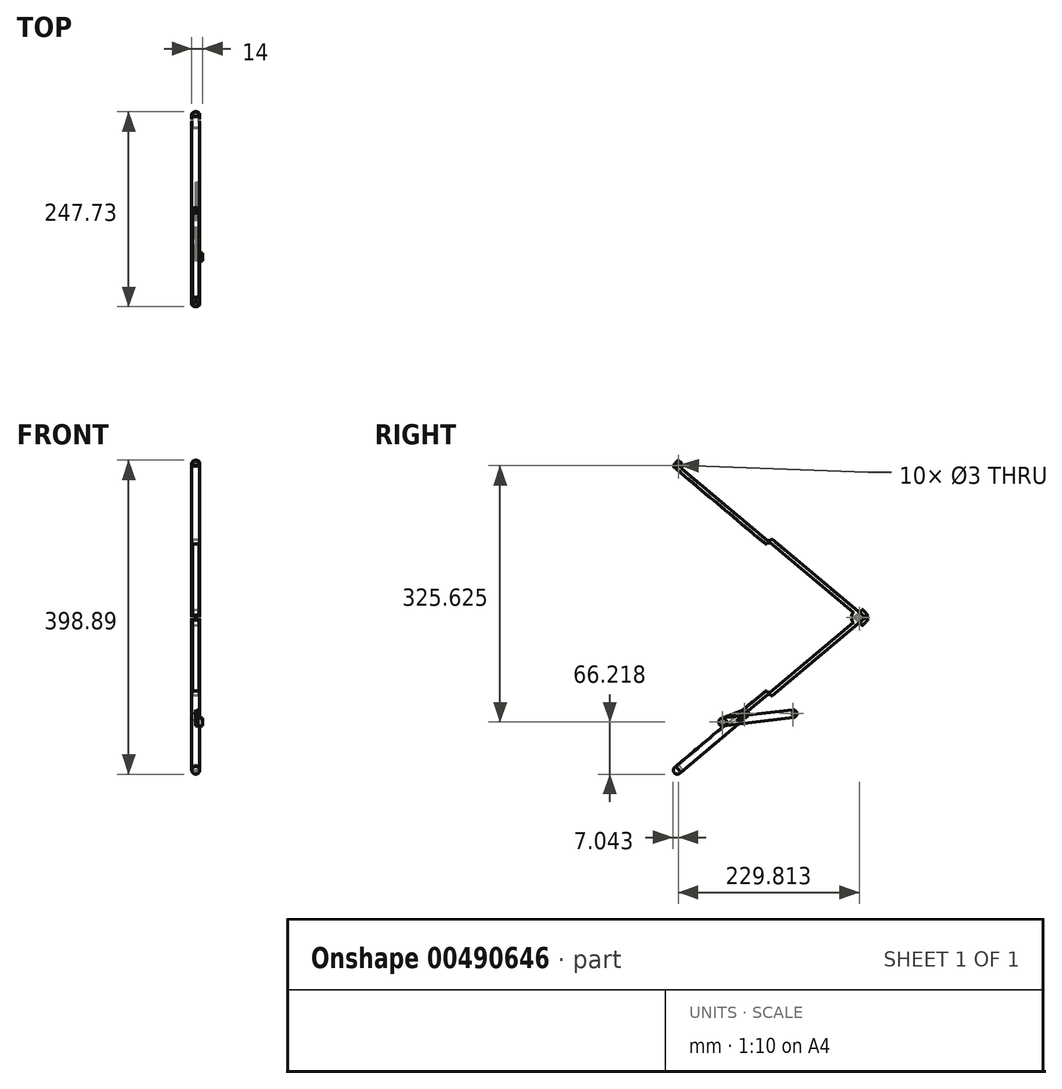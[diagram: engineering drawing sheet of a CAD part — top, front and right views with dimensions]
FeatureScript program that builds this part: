
annotation { "Feature Type Name" : "Feature", "Feature Type Description" : "" }
export const myFeature = defineFeature(function(context is Context, id is Id, definition is map)
    precondition{}
    {
        {
            assignVariable(context, id + "F0", {"name" : "tube_od", "anyValue" : 10});
        }
        {
            var Q0;
            Q0=qCreatedBy(makeId("Right.planeOp"),FACE);
            var sketch = newSketch(context, id + "F1", { "sketchPlane" : qUnion([Q0])});
            skLineSegment(sketch, "E0", {"start": v(114.9, 0) * mm, "end": v(114.9, 664.57) * mm, "construction": true});
            skLineSegment(sketch, "E1", {"start": v(-114.9, 0) * mm, "end": v(-114.9, 664.3) * mm, "construction": true});
            skLineSegment(sketch, "E2", {"start": v(114.9, 5) * mm, "end": v(-114.9, 197.84) * mm});
            skLineSegment(sketch, "E3", {"start": v(-114.9, 197.84) * mm, "end": v(114.9, 390.67) * mm});
            skLineSegment(sketch, "E4", {"start": v(-114.9, 5) * mm, "end": v(114.9, 5) * mm, "construction": true});
            skLineSegment(sketch, "E5", {"start": v(-114.9, 5) * mm, "end": v(114.9, 197.84) * mm});
            skLineSegment(sketch, "E6", {"start": v(114.9, 197.84) * mm, "end": v(-114.9, 390.67) * mm});
            skPoint(sketch, "E7", {"position": v(0, 5) * mm});
            skCircle(sketch, "E8", {"center": v(114.9, 5) * mm, "radius": 5 * mm});
            skLineSegment(sketch, "E9", {"start": v(114.9, 390.67) * mm, "end": v(-114.9, 583.5) * mm});
            skLineSegment(sketch, "E10", {"start": v(-114.9, 390.67) * mm, "end": v(114.9, 583.5) * mm});
            skLineSegment(sketch, "E11", {"start": v(-30.64, 75.7) * mm, "end": v(30.64, 75.7) * mm, "construction": true});
            skLineSegment(sketch, "E12", {"start": v(-30.64, 75.7) * mm, "end": v(-58.68, 65.05) * mm});
            skLineSegment(sketch, "E13", {"start": v(-58.68, 65.05) * mm, "end": v(30.64, 75.7) * mm});
            skPoint(sketch, "E14", {"position": v(0, 101.42) * mm});
            skCircle(sketch, "E15", {"center": v(-30.64, 75.7) * mm, "radius": 30 * mm, "construction": true});
            skPoint(sketch, "E16", {"position": v(-53.62, 56.42) * mm});
            skCircle(sketch, "E17", {"center": v(-53.62, 56.42) * mm, "radius": 5 * mm});
            skCircle(sketch, "E18", {"center": v(-58.68, 65.05) * mm, "radius": 5 * mm});
            skCircle(sketch, "E19", {"center": v(114.9, 197.84) * mm, "radius": 10 * mm});
            skLineSegment(sketch, "E20", {"start": v(114.9, 197.84) * mm, "end": v(122.57, 204.26) * mm});
            skLineSegment(sketch, "E21", {"start": v(114.9, 197.84) * mm, "end": v(122.57, 191.4) * mm});
            skCircle(sketch, "E22", {"center": v(-114.9, 390.67) * mm, "radius": 5 * mm});
            skLineSegment(sketch, "E23", {"start": v(-114.9, 390.67) * mm, "end": v(-118.74, 393.89) * mm});
            skLineSegment(sketch, "E24", {"start": v(-114.9, 5) * mm, "end": v(-111.7, 1.17) * mm});
            skLineSegment(sketch, "E25", {"start": v(-111.7, 1.17) * mm, "end": v(-113.09, 0) * mm});
            skLineSegment(sketch, "E26", {"start": v(-112.34, 1.94) * mm, "end": v(-109.27, 4.5) * mm});
            skLineSegment(sketch, "E27", {"start": v(-109.27, 4.5) * mm, "end": v(-111.84, 7.57) * mm});
            skArc(sketch, "E28", {"start": v(-113.09, 0) * mm, "mid": v(-116.74, -1.15) * mm, "end": v(-120.13, 0.62) * mm});
            skLineSegment(sketch, "E29", {"start": v(-120.13, 0.62) * mm, "end": v(-114.9, 5) * mm});
            skCircle(sketch, "E30", {"center": v(114.9, 197.84) * mm, "radius": 1.5 * mm});
            skCircle(sketch, "E31", {"center": v(0, 101.42) * mm, "radius": 1.5 * mm});
            skCircle(sketch, "E32", {"center": v(0, 294.25) * mm, "radius": 1.5 * mm});
            skCircle(sketch, "E33", {"center": v(-114.9, 390.67) * mm, "radius": 1.5 * mm});
            skSolve(sketch);
        }
        {
            var Q0;
            Q0=sQuery(id+"F1.wireOp",VERTEX,"E5.start");
            var Q1;
            Q1=sQuery(id+"F1.wireOp",EDGE,"E5");
            cPlane(context, id + "F2", {"entities" : qUnion([Q0, Q1]), "cplaneType" : CPlaneType.LINE_POINT, "offset" : 25 * mm, "width" : 150 * mm, "height" : 150 * mm});
        }
        {
            var Q0;
            Q0=qCreatedBy(id+"F2.planeOp",FACE);
            var sketch = newSketch(context, id + "F3", { "sketchPlane" : qUnion([Q0])});
            skPoint(sketch, "E34.0", {"position": v(0, 77.7) * mm});
            skCircle(sketch, "E35", {"center": v(0, 77.7) * mm, "radius": 5 * mm});
            skCircle(sketch, "E36", {"center": v(0, 77.7) * mm, "radius": 4 * mm});
            skSolve(sketch);
        }
        {
            var Q0;
            Q0=makeQuery(id+"F3.imprint","IMPRINT",FACE,{"disambiguationData":[TD([[makeQuery(id+"F3.imprint","IMPRINT",EDGE,{"derivedFrom":sQuery(id+"F3.wireOp",EDGE,"E35")}),1.0]])]});
            var Q1;
            Q1=sQuery(id+"F1.wireOp",EDGE,"E5");
            var Q2;
            Q2=sQuery(id+"F1.wireOp",EDGE,"E20");
            sweep(context, id + "F4", {"profiles" : qUnion([Q0]), "path" : qUnion([Q1, Q2])});
        }
        {
            var Q0;
            Q0=sQuery(id+"F1.wireOp",VERTEX,"E21.end");
            var Q1;
            Q1=sQuery(id+"F1.wireOp",EDGE,"E6");
            cPlane(context, id + "F5", {"entities" : qUnion([Q0, Q1]), "cplaneType" : CPlaneType.LINE_POINT, "offset" : 25 * mm, "width" : 150 * mm, "height" : 150 * mm});
        }
        {
            var Q0;
            Q0=qCreatedBy(id+"F5.planeOp",FACE);
            var sketch = newSketch(context, id + "F6", { "sketchPlane" : qUnion([Q0])});
            skPoint(sketch, "E37.0", {"position": v(0, 225.41) * mm});
            skCircle(sketch, "E38", {"center": v(0, 225.41) * mm, "radius": 5 * mm});
            skCircle(sketch, "E39", {"center": v(0, 225.41) * mm, "radius": 4 * mm});
            skSolve(sketch);
        }
        {
            var Q0;
            Q0=makeQuery(id+"F6.imprint","IMPRINT",FACE,{"disambiguationData":[TD([[makeQuery(id+"F6.imprint","IMPRINT",EDGE,{"derivedFrom":sQuery(id+"F6.wireOp",EDGE,"E38")}),1.0]])]});
            var Q1;
            Q1=sQuery(id+"F1.wireOp",EDGE,"E21");
            var Q2;
            Q2=sQuery(id+"F1.wireOp",EDGE,"E6");
            var Q3;
            Q3=sQuery(id+"F1.wireOp",EDGE,"E23");
            sweep(context, id + "F7", {"profiles" : qUnion([Q0]), "path" : qUnion([Q1, Q2, Q3])});
        }
        {
            var Q0;
            {var subQ0=sQuery(id+"F1.wireOp",EDGE,"E25");Q0=makeQuery(id+"F1.imprint","IMPRINT",FACE,{"disambiguationData":[TD([[makeQuery(id+"F1.imprint","IMPRINT",EDGE,{"derivedFrom":subQ0}),-1.0]])]});}
            var Q1;
            {var subQ4=sQuery(id+"F1.wireOp",EDGE,"E26");Q1=makeQuery(id+"F1.imprint","IMPRINT",FACE,{"disambiguationData":[TD([[makeQuery(id+"F1.imprint","IMPRINT",EDGE,{"derivedFrom":subQ4}),1.0]])]});}
            var Q2;
            Q2=sQuery(id+"F1.wireOp",EDGE,"E5");
            revolve(context, id + "F8", {"entities" : qUnion([Q0, Q1]), "axis" : qUnion([Q2]), "revolveType" : RevolveType.FULL});
        }
        {
            var Q0;
            {var subQ0=sQuery(id+"F1.wireOp",EDGE,"E31");var subQ1=sQuery(id+"F1.wireOp",EDGE,"E2");var subQ2=makeQuery(id+"F1.imprint","INTERSECT",VERTEX,{"disambiguationData":[OD(1.0)],"derivedFrom":[subQ1,subQ0]});Q0=makeQuery(id+"F1.imprint","IMPRINT",FACE,{"disambiguationData":[TD([[makeQuery(id+"F1.imprint","IMPRINT",EDGE,{"disambiguationData":[TD([[subQ2,1.0]])],"derivedFrom":subQ1}),1.0]])]});}
            var Q1;
            {var subQ0=sQuery(id+"F1.wireOp",EDGE,"E31");var subQ1=sQuery(id+"F1.wireOp",EDGE,"E2");var subQ2=makeQuery(id+"F1.imprint","INTERSECT",VERTEX,{"disambiguationData":[OD(1.0)],"derivedFrom":[subQ1,subQ0]});Q1=makeQuery(id+"F1.imprint","IMPRINT",FACE,{"disambiguationData":[TD([[makeQuery(id+"F1.imprint","IMPRINT",EDGE,{"disambiguationData":[TD([[subQ2,1.0]])],"derivedFrom":subQ1}),-1.0]])]});}
            var Q2;
            {var subQ0=sQuery(id+"F1.wireOp",EDGE,"E31");var subQ1=sQuery(id+"F1.wireOp",EDGE,"E2");var subQ2=makeQuery(id+"F1.imprint","INTERSECT",VERTEX,{"disambiguationData":[OD(0.0)],"derivedFrom":[subQ1,subQ0]});Q2=makeQuery(id+"F1.imprint","IMPRINT",FACE,{"disambiguationData":[TD([[makeQuery(id+"F1.imprint","IMPRINT",EDGE,{"disambiguationData":[TD([[subQ2,-1.0]])],"derivedFrom":subQ1}),-1.0]])]});}
            var Q3;
            {var subQ0=sQuery(id+"F1.wireOp",EDGE,"E31");var subQ1=sQuery(id+"F1.wireOp",EDGE,"E2");var subQ2=makeQuery(id+"F1.imprint","INTERSECT",VERTEX,{"disambiguationData":[OD(0.0)],"derivedFrom":[subQ1,subQ0]});Q3=makeQuery(id+"F1.imprint","IMPRINT",FACE,{"disambiguationData":[TD([[makeQuery(id+"F1.imprint","IMPRINT",EDGE,{"disambiguationData":[TD([[subQ2,-1.0]])],"derivedFrom":subQ1}),1.0]])]});}
            var Q4;
            {var subQ1=sQuery(id+"F1.wireOp",EDGE,"E5");var subQ3=sQuery(id+"F1.wireOp",EDGE,"E30");var subQ4=makeQuery(id+"F1.imprint","INTERSECT",VERTEX,{"derivedFrom":[subQ1,subQ3]});Q4=makeQuery(id+"F1.imprint","IMPRINT",FACE,{"disambiguationData":[TD([[makeQuery(id+"F1.imprint","IMPRINT",EDGE,{"disambiguationData":[TD([[subQ4,1.0]])],"derivedFrom":subQ3}),1.0]])]});}
            var Q5;
            {var subQ1=sQuery(id+"F1.wireOp",EDGE,"E6");var subQ3=sQuery(id+"F1.wireOp",EDGE,"E30");var subQ4=makeQuery(id+"F1.imprint","INTERSECT",VERTEX,{"derivedFrom":[subQ1,subQ3]});Q5=makeQuery(id+"F1.imprint","IMPRINT",FACE,{"disambiguationData":[TD([[makeQuery(id+"F1.imprint","IMPRINT",EDGE,{"disambiguationData":[TD([[subQ4,1.0]])],"derivedFrom":subQ3}),1.0]])]});}
            var Q6;
            {var subQ1=sQuery(id+"F1.wireOp",EDGE,"E20");var subQ3=sQuery(id+"F1.wireOp",EDGE,"E30");var subQ4=makeQuery(id+"F1.imprint","INTERSECT",VERTEX,{"derivedFrom":[subQ1,subQ3]});Q6=makeQuery(id+"F1.imprint","IMPRINT",FACE,{"disambiguationData":[TD([[makeQuery(id+"F1.imprint","IMPRINT",EDGE,{"disambiguationData":[TD([[subQ4,1.0]])],"derivedFrom":subQ3}),1.0]])]});}
            var Q7;
            {var subQ1=sQuery(id+"F1.wireOp",EDGE,"E5");var subQ3=sQuery(id+"F1.wireOp",EDGE,"E30");var subQ4=makeQuery(id+"F1.imprint","INTERSECT",VERTEX,{"derivedFrom":[subQ1,subQ3]});Q7=makeQuery(id+"F1.imprint","IMPRINT",FACE,{"disambiguationData":[TD([[makeQuery(id+"F1.imprint","IMPRINT",EDGE,{"disambiguationData":[TD([[subQ4,-1.0]])],"derivedFrom":subQ3}),1.0]])]});}
            var Q8;
            {var subQ0=sQuery(id+"F1.wireOp",EDGE,"E32");var subQ1=sQuery(id+"F1.wireOp",EDGE,"E3");var subQ2=makeQuery(id+"F1.imprint","INTERSECT",VERTEX,{"disambiguationData":[OD(0.0)],"derivedFrom":[subQ1,subQ0]});Q8=makeQuery(id+"F1.imprint","IMPRINT",FACE,{"disambiguationData":[TD([[makeQuery(id+"F1.imprint","IMPRINT",EDGE,{"disambiguationData":[TD([[subQ2,-1.0]])],"derivedFrom":subQ1}),1.0]])]});}
            var Q9;
            {var subQ0=sQuery(id+"F1.wireOp",EDGE,"E32");var subQ1=sQuery(id+"F1.wireOp",EDGE,"E3");var subQ2=makeQuery(id+"F1.imprint","INTERSECT",VERTEX,{"disambiguationData":[OD(1.0)],"derivedFrom":[subQ1,subQ0]});Q9=makeQuery(id+"F1.imprint","IMPRINT",FACE,{"disambiguationData":[TD([[makeQuery(id+"F1.imprint","IMPRINT",EDGE,{"disambiguationData":[TD([[subQ2,1.0]])],"derivedFrom":subQ1}),1.0]])]});}
            var Q10;
            {var subQ0=sQuery(id+"F1.wireOp",EDGE,"E32");var subQ1=sQuery(id+"F1.wireOp",EDGE,"E3");var subQ2=makeQuery(id+"F1.imprint","INTERSECT",VERTEX,{"disambiguationData":[OD(1.0)],"derivedFrom":[subQ1,subQ0]});Q10=makeQuery(id+"F1.imprint","IMPRINT",FACE,{"disambiguationData":[TD([[makeQuery(id+"F1.imprint","IMPRINT",EDGE,{"disambiguationData":[TD([[subQ2,1.0]])],"derivedFrom":subQ1}),-1.0]])]});}
            var Q11;
            {var subQ0=sQuery(id+"F1.wireOp",EDGE,"E32");var subQ1=sQuery(id+"F1.wireOp",EDGE,"E3");var subQ2=makeQuery(id+"F1.imprint","INTERSECT",VERTEX,{"disambiguationData":[OD(0.0)],"derivedFrom":[subQ1,subQ0]});Q11=makeQuery(id+"F1.imprint","IMPRINT",FACE,{"disambiguationData":[TD([[makeQuery(id+"F1.imprint","IMPRINT",EDGE,{"disambiguationData":[TD([[subQ2,-1.0]])],"derivedFrom":subQ1}),-1.0]])]});}
            var Q12;
            {var subQ1=sQuery(id+"F1.wireOp",EDGE,"E6");var subQ3=sQuery(id+"F1.wireOp",EDGE,"E33");var subQ4=makeQuery(id+"F1.imprint","INTERSECT",VERTEX,{"derivedFrom":[subQ1,subQ3]});Q12=makeQuery(id+"F1.imprint","IMPRINT",FACE,{"disambiguationData":[TD([[makeQuery(id+"F1.imprint","IMPRINT",EDGE,{"disambiguationData":[TD([[subQ4,1.0]])],"derivedFrom":subQ3}),1.0]])]});}
            var Q13;
            {var subQ1=sQuery(id+"F1.wireOp",EDGE,"E10");var subQ3=sQuery(id+"F1.wireOp",EDGE,"E33");var subQ4=makeQuery(id+"F1.imprint","INTERSECT",VERTEX,{"derivedFrom":[subQ1,subQ3]});Q13=makeQuery(id+"F1.imprint","IMPRINT",FACE,{"disambiguationData":[TD([[makeQuery(id+"F1.imprint","IMPRINT",EDGE,{"disambiguationData":[TD([[subQ4,-1.0]])],"derivedFrom":subQ3}),1.0]])]});}
            var Q14;
            {var subQ1=sQuery(id+"F1.wireOp",EDGE,"E6");var subQ3=sQuery(id+"F1.wireOp",EDGE,"E33");var subQ4=makeQuery(id+"F1.imprint","INTERSECT",VERTEX,{"derivedFrom":[subQ1,subQ3]});Q14=makeQuery(id+"F1.imprint","IMPRINT",FACE,{"disambiguationData":[TD([[makeQuery(id+"F1.imprint","IMPRINT",EDGE,{"disambiguationData":[TD([[subQ4,-1.0]])],"derivedFrom":subQ3}),1.0]])]});}
            extrude(context, id + "F9", {"entities" : qUnion([Q0, Q1, Q2, Q3, Q4, Q5, Q6, Q7, Q8, Q9, Q10, Q11, Q12, Q13, Q14]), "operationType" : NewBodyOperationType.REMOVE, "endBound" : BoundingType.SYMMETRIC, "oppositeDirection" : true, "depth" : 25 * mm});
        }
        {
            var Q0;
            Q0=qCreatedBy(makeId("Right.planeOp"),FACE);
            var sketch = newSketch(context, id + "F10", { "sketchPlane" : qUnion([Q0])});
            skPoint(sketch, "E40.0", {"position": v(-30.64, 75.7) * mm});
            skPoint(sketch, "E41.0", {"position": v(-58.68, 65.05) * mm});
            skCircle(sketch, "E42", {"center": v(-30.64, 75.7) * mm, "radius": 1.5 * mm});
            skCircle(sketch, "E43", {"center": v(-58.68, 65.05) * mm, "radius": 1.5 * mm});
            skLineSegment(sketch, "E44.0", {"start": v(-30.64, 75.7) * mm, "end": v(-58.68, 65.05) * mm});
            skArc(sketch, "E45.0.startCap", {"start": v(-32.42, 80.38) * mm, "mid": v(-25.97, 77.48) * mm, "end": v(-28.87, 71.03) * mm});
            skArc(sketch, "E45.0.endCap", {"start": v(-56.9, 60.37) * mm, "mid": v(-63.36, 63.27) * mm, "end": v(-60.46, 69.72) * mm});
            skLineSegment(sketch, "E45.0.left", {"start": v(-28.87, 71.03) * mm, "end": v(-56.9, 60.37) * mm});
            skLineSegment(sketch, "E45.0.right", {"start": v(-32.42, 80.38) * mm, "end": v(-60.46, 69.72) * mm});
            skSolve(sketch);
        }
        {
            var Q0;
            Q0=makeQuery(id+"F10.imprint","IMPRINT",FACE,{"disambiguationData":[TD([[makeQuery(id+"F10.imprint","IMPRINT",EDGE,{"derivedFrom":sQuery(id+"F10.wireOp",EDGE,"E42")}),-1.0]])]});
            extrude(context, id + "F11", {"entities" : qUnion([Q0]), "depth" : 2.5 * mm});
        }
        {
            var Q0;
            Q0=qCreatedBy(makeId("Right.planeOp"),FACE);
            var sketch = newSketch(context, id + "F12", { "sketchPlane" : qUnion([Q0])});
            skLineSegment(sketch, "E46.0", {"start": v(-58.68, 65.05) * mm, "end": v(30.64, 75.7) * mm});
            skCircle(sketch, "E47", {"center": v(-58.68, 65.05) * mm, "radius": 1.5 * mm});
            skCircle(sketch, "E48", {"center": v(30.64, 75.7) * mm, "radius": 1.5 * mm});
            skArc(sketch, "E49.0.startCap", {"start": v(-58.1, 60.08) * mm, "mid": v(-63.65, 64.46) * mm, "end": v(-59.28, 70.01) * mm});
            skArc(sketch, "E49.0.endCap", {"start": v(30.05, 80.67) * mm, "mid": v(35.6, 76.3) * mm, "end": v(31.23, 70.74) * mm});
            skLineSegment(sketch, "E49.0.left", {"start": v(-59.28, 70.01) * mm, "end": v(30.05, 80.67) * mm});
            skLineSegment(sketch, "E49.0.right", {"start": v(-58.1, 60.08) * mm, "end": v(31.23, 70.74) * mm});
            skSolve(sketch);
        }
        {
            var Q0;
            Q0=makeQuery(id+"F12.imprint","IMPRINT",FACE,{"disambiguationData":[TD([[makeQuery(id+"F12.imprint","IMPRINT",EDGE,{"derivedFrom":sQuery(id+"F12.wireOp",EDGE,"E47")}),-1.0]])]});
            extrude(context, id + "F13", {"entities" : qUnion([Q0]), "depth" : 2.5 * mm});
        }
        {
            var Q0;
            Q0=makeQuery(id+"F10.imprint","IMPRINT",FACE,{"disambiguationData":[TD([[makeQuery(id+"F10.imprint","IMPRINT",EDGE,{"derivedFrom":sQuery(id+"F10.wireOp",EDGE,"E42")}),1.0]])]});
            extrude(context, id + "F14", {"entities" : qUnion([Q0]), "operationType" : NewBodyOperationType.REMOVE, "endBound" : BoundingType.SYMMETRIC, "oppositeDirection" : true, "depth" : 25 * mm});
        }
        {
            var Q0;
            {var subQ0=sQuery(id+"F1.wireOp",EDGE,"E13");var subQ1=sQuery(id+"F1.wireOp",EDGE,"E12");var subQ2=makeQuery(id+"F1.imprint","INTERSECT",VERTEX,{"derivedFrom":[subQ1,subQ0]});Q0=makeQuery(id+"F1.imprint","IMPRINT",FACE,{"disambiguationData":[TD([[makeQuery(id+"F1.imprint","IMPRINT",EDGE,{"disambiguationData":[TD([[subQ2,1.0]])],"derivedFrom":subQ1}),-1.0]])]});}
            var Q1;
            {var subQ0=sQuery(id+"F1.wireOp",EDGE,"E13");var subQ1=sQuery(id+"F1.wireOp",EDGE,"E12");var subQ2=makeQuery(id+"F1.imprint","INTERSECT",VERTEX,{"derivedFrom":[subQ1,subQ0]});Q1=makeQuery(id+"F1.imprint","IMPRINT",FACE,{"disambiguationData":[TD([[makeQuery(id+"F1.imprint","IMPRINT",EDGE,{"disambiguationData":[TD([[subQ2,1.0]])],"derivedFrom":subQ1}),1.0]])]});}
            extrude(context, id + "F15", {"entities" : qUnion([Q0, Q1]), "depth" : (0.9 * getVariable(context, 'tube_od')) * mm});
        }
    });
